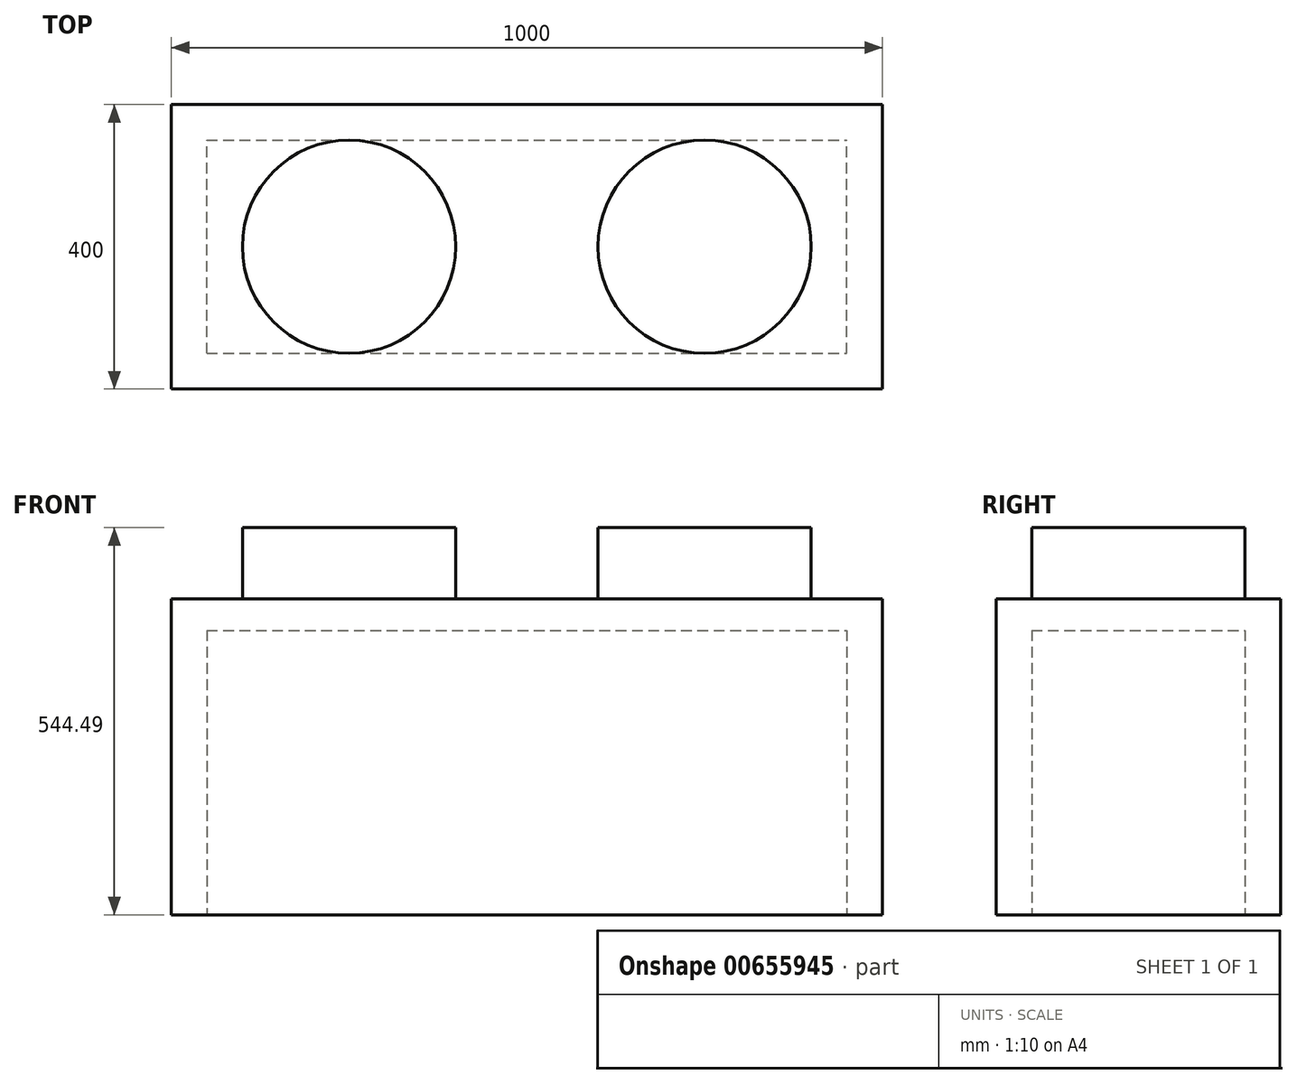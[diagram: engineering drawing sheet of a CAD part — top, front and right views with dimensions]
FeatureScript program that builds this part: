
annotation { "Feature Type Name" : "Feature", "Feature Type Description" : "" }
export const myFeature = defineFeature(function(context is Context, id is Id, definition is map)
    precondition{}
    {
        {
            var Q0;
            Q0=qCreatedBy(makeId("Front.planeOp"),FACE);
            var sketch = newSketch(context, id + "F0", { "sketchPlane" : qUnion([Q0])});
            skLineSegment(sketch, "E0.bottom", {"start": v(-1031.68, 397.2) * mm, "end": v(-31.68, 397.2) * mm});
            skLineSegment(sketch, "E0.left", {"start": v(-1031.68, 397.2) * mm, "end": v(-1031.68, -2.8) * mm});
            skLineSegment(sketch, "E0.right", {"start": v(-31.68, 397.2) * mm, "end": v(-31.68, 52.7) * mm});
            skLineSegment(sketch, "E1", {"start": v(-1031.68, 397.2) * mm, "end": v(-931.68, 397.2) * mm});
            skLineSegment(sketch, "E2", {"start": v(-931.68, 397.2) * mm, "end": v(-931.68, 497.2) * mm});
            skLineSegment(sketch, "E3", {"start": v(-931.68, 497.2) * mm, "end": v(-631.68, 497.2) * mm});
            skLineSegment(sketch, "E4", {"start": v(-631.68, 497.2) * mm, "end": v(-631.68, 397.2) * mm});
            skLineSegment(sketch, "E5", {"start": v(-31.68, 397.2) * mm, "end": v(-131.68, 397.2) * mm});
            skLineSegment(sketch, "E6", {"start": v(-131.68, 397.2) * mm, "end": v(-131.68, 497.2) * mm});
            skLineSegment(sketch, "E7", {"start": v(-131.68, 497.2) * mm, "end": v(-431.68, 497.2) * mm});
            skLineSegment(sketch, "E8", {"start": v(-431.68, 497.2) * mm, "end": v(-431.68, 397.2) * mm});
            skLineSegment(sketch, "E9", {"start": v(-31.68, 52.7) * mm, "end": v(-31.68, -47.3) * mm});
            skLineSegment(sketch, "E10", {"start": v(-31.68, -47.3) * mm, "end": v(-1031.68, -47.3) * mm});
            skLineSegment(sketch, "E11", {"start": v(-1031.68, -47.3) * mm, "end": v(-1031.68, -2.8) * mm});
            skSolve(sketch);
        }
        {
            var Q0;
            Q0=makeQuery(id+"F0.imprint","IMPRINT",FACE,{"disambiguationData":[TD([[makeQuery(id+"F0.imprint","IMPRINT",EDGE,{"derivedFrom":sQuery(id+"F0.wireOp",EDGE,"E0.left")}),1.0]])]});
            extrude(context, id + "F1", {"entities" : qUnion([Q0]), "oppositeDirection" : true, "depth" : 400 * mm, "offsetDistance" : 25 * mm});
        }
        {
            var Q0;
            Q0=makeQuery(id+"F1.opExtrude","SWEPT_FACE",FACE,{"disambiguationData":[OSD([sQuery(id+"F0.wireOp",EDGE,"E0.bottom"),sQuery(id+"F0.wireOp",EDGE,"E1"),sQuery(id+"F0.wireOp",EDGE,"E5")])]});
            var sketch = newSketch(context, id + "F2", { "sketchPlane" : qUnion([Q0])});
            skLineSegment(sketch, "E12", {"start": v(-1031.68, 400) * mm, "end": v(-1031.68, 200) * mm});
            skCircle(sketch, "E13", {"center": v(-781.68, 200) * mm, "radius": 150 * mm});
            skCircle(sketch, "E14", {"center": v(-281.68, 200) * mm, "radius": 150 * mm});
            skSolve(sketch);
        }
        {
            var Q0;
            Q0 = qSketchRegion(id + "F2", true);
            extrude(context, id + "F3", {"entities" : qUnion([Q0]), "operationType" : NewBodyOperationType.ADD, "depth" : 100 * mm, "offsetDistance" : 25 * mm});
        }
        {
            var Q0;
            Q0=makeQuery(id+"F1.opExtrude","SWEPT_FACE",FACE,{"disambiguationData":[OSD([sQuery(id+"F0.wireOp",EDGE,"E10")])]});
            var sketch = newSketch(context, id + "F4", { "sketchPlane" : qUnion([Q0])});
            skLineSegment(sketch, "E15", {"start": v(-1031.68, 0) * mm, "end": v(-1031.68, -50) * mm});
            skLineSegment(sketch, "E16", {"start": v(-1031.68, -50) * mm, "end": v(-981.68, -50) * mm});
            skLineSegment(sketch, "E17.bottom", {"start": v(-981.68, -50) * mm, "end": v(-81.68, -50) * mm});
            skLineSegment(sketch, "E17.top", {"start": v(-981.68, -350) * mm, "end": v(-81.68, -350) * mm});
            skLineSegment(sketch, "E17.left", {"start": v(-981.68, -50) * mm, "end": v(-981.68, -350) * mm});
            skLineSegment(sketch, "E17.right", {"start": v(-81.68, -50) * mm, "end": v(-81.68, -350) * mm});
            skSolve(sketch);
        }
        {
            var Q0;
            Q0 = qSketchRegion(id + "F4", true);
            extrude(context, id + "F5", {"entities" : qUnion([Q0]), "operationType" : NewBodyOperationType.REMOVE, "oppositeDirection" : true, "depth" : 400 * mm, "offsetDistance" : 25 * mm});
        }
    });
